# Revit family: QF_COMCATER ALL BRANDS_RCR6-2-3G
name_source: partatom
category: Specialty Equipment
revit_build: Autodesk Revit 2014 (Build: 20140709_2115(x64)
units: mm (PartAtom-declared; Revit-internal decimal feet)

## types (2) — shared parameters
Accessory = No
Assembly Code = E1090320
BTUH = 21300 W
Depth Actual = 830 mm  [stored 2.7231 ft]
Description = 2 BURNER COMBINATION RANGE WITH OVEN
Gas Flow = 0.0 L/s
Gas Size = 19 mm
Gas Size Flexible = 0 mm
Gas power kW = 21.3
Height Actual = 1135 mm  [stored 3.72375 ft]
Length Actual = 600 mm  [stored 1.9685 ft]
Manufacturer = TRUEHEAT
Model = RCR6-2-3G
Nominal Gas power = 21300 W
Type Comments = The Australian owned and designed* Trueheat RC Series of Gas Cooking Equipment has been developed for the restaurant and cafe market with a high quality finish, designed to fulfill the busy demands within a commercial kitchen.
Powerful 24MJ/hr open burners with individual standing pilots included.
100% Flame failure controls included as standard. Matt finish premium look cast iron trivets radiant heat and design makes it easy to move pots around the surface.
16mm thick steel griddle plate with 16.5MJ/hr burner per 300mm section.
25MJ/hr static oven with two oven racks fit to removable vertical rack guides which provide 3 rack heights. Oven racks are fabricated from 304 stainless steel. Interior oven panels are coated with black vitreous enamel for ease of cleaning.
Note: Griddle is convertible to the left hand side. Additional charges apply.

## type names (no varying parameters)
- RCR6-2-3G_Natural Gas
- RCR6-2-3G_LPG

note: [stored X ft] marks values corroborated as IEEE doubles in the binary element streams (Revit-internal decimal feet)

## geometry (parser evidence)
native form markers: Sweep x6
no freeform markers — native parametric forms only
